# Revit family: 1FJVR Sensor_RFA
name_source: partatom
category: Pipe Accessories
units: mm (PartAtom-declared; Revit-internal decimal feet)

## family parameters
Always vertical = Yes
Cut with Voids When Loaded = No
OmniClass Number = 23.65.55.14.17
OmniClass Title = Adjusting/Controlling Valves for Liquid Services
Part Type = Normal
Round Connector Dimension = Use Diameter
Shared = Yes
Work Plane-Based = No

## types (2) — shared parameters
Body Material = Danfoss Plastic White
Description = Radiator Sensor
IfcExportAs = IfcActuatorType
IfcExportType = FJVR
LOD 200 = No
LOD 350 = Yes
Manufacturer = Danfoss
Min Temperature Setting = 10 °C
URL = https://store.danfoss.com
Weight = 0.14 kg

## per-type parameters (varying)
| type | Max Temperature Setting | Model |
| FJVR Sensor_10-50 °C | 50 °C | 003L1040,003L1047 |
| FJVR Sensor_10-80 °C | 80 °C | 003L1070,003L1070S,003L1077 |

note: column(s) folded — value = type name in every type: Model Type

## geometry (parser evidence)
native form markers: Sweep x1
no freeform markers — native parametric forms only
